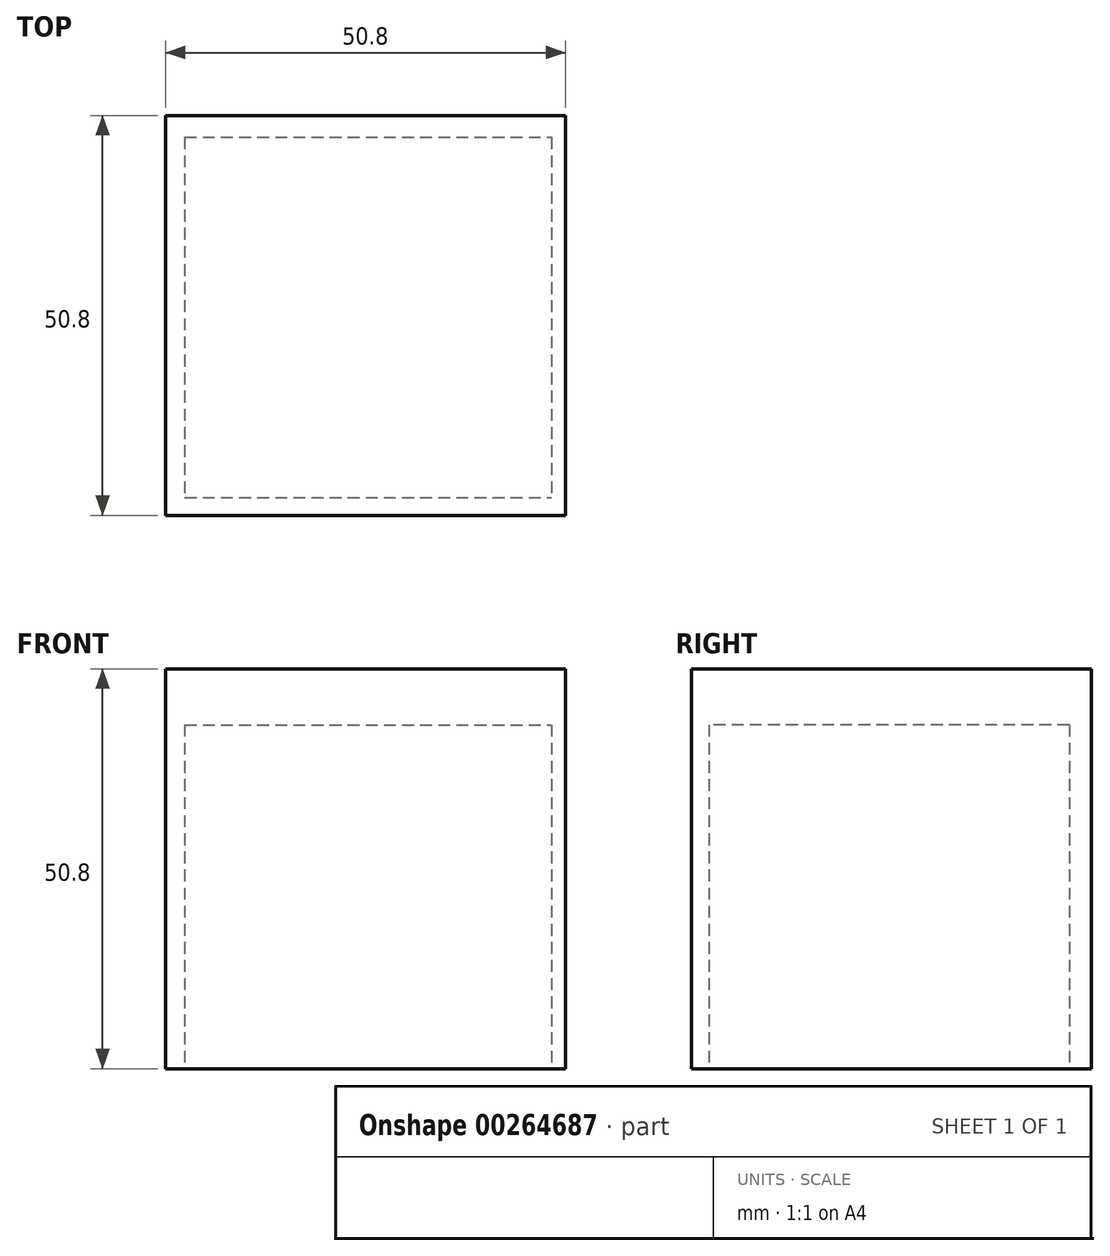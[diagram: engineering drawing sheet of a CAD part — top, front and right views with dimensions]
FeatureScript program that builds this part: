
annotation { "Feature Type Name" : "Feature", "Feature Type Description" : "" }
export const myFeature = defineFeature(function(context is Context, id is Id, definition is map)
    precondition{}
    {
        {
            var Q0;
            Q0=qCreatedBy(makeId("Front.planeOp"),FACE);
            var sketch = newSketch(context, id + "F0", { "sketchPlane" : qUnion([Q0])});
            skLineSegment(sketch, "E0.bottom", {"start": v(0, 0) * mm, "end": v(-50.8, 0) * mm});
            skLineSegment(sketch, "E0.top", {"start": v(0, 50.8) * mm, "end": v(-50.8, 50.8) * mm});
            skLineSegment(sketch, "E0.left", {"start": v(0, 0) * mm, "end": v(0, 50.8) * mm});
            skLineSegment(sketch, "E0.right", {"start": v(-50.8, 0) * mm, "end": v(-50.8, 50.8) * mm});
            skSolve(sketch);
        }
        {
            var Q0;
            Q0 = qSketchRegion(id + "F0", true);
            extrude(context, id + "F1", {"entities" : qUnion([Q0]), "depth" : 50.8 * mm});
        }
        {
            var Q0;
            Q0=qCreatedBy(makeId("Top.planeOp"),FACE);
            var sketch = newSketch(context, id + "F2", { "sketchPlane" : qUnion([Q0])});
            skLineSegment(sketch, "E1.bottom", {"start": v(-48.36, -2.79) * mm, "end": v(-1.8, -2.79) * mm});
            skLineSegment(sketch, "E1.top", {"start": v(-48.36, -48.56) * mm, "end": v(-1.8, -48.56) * mm});
            skLineSegment(sketch, "E1.left", {"start": v(-48.36, -2.79) * mm, "end": v(-48.36, -48.56) * mm});
            skLineSegment(sketch, "E1.right", {"start": v(-1.8, -2.79) * mm, "end": v(-1.8, -48.56) * mm});
            skSolve(sketch);
        }
        {
            var Q0;
            Q0=makeQuery(id+"F2.imprint","IMPRINT",FACE,{"disambiguationData":[TD([[makeQuery(id+"F2.imprint","IMPRINT",EDGE,{"derivedFrom":sQuery(id+"F2.wireOp",EDGE,"E1.bottom")}),-1.0]])]});
            extrude(context, id + "F3", {"entities" : qUnion([Q0]), "operationType" : NewBodyOperationType.REMOVE, "depth" : 43.69 * mm});
        }
    });
